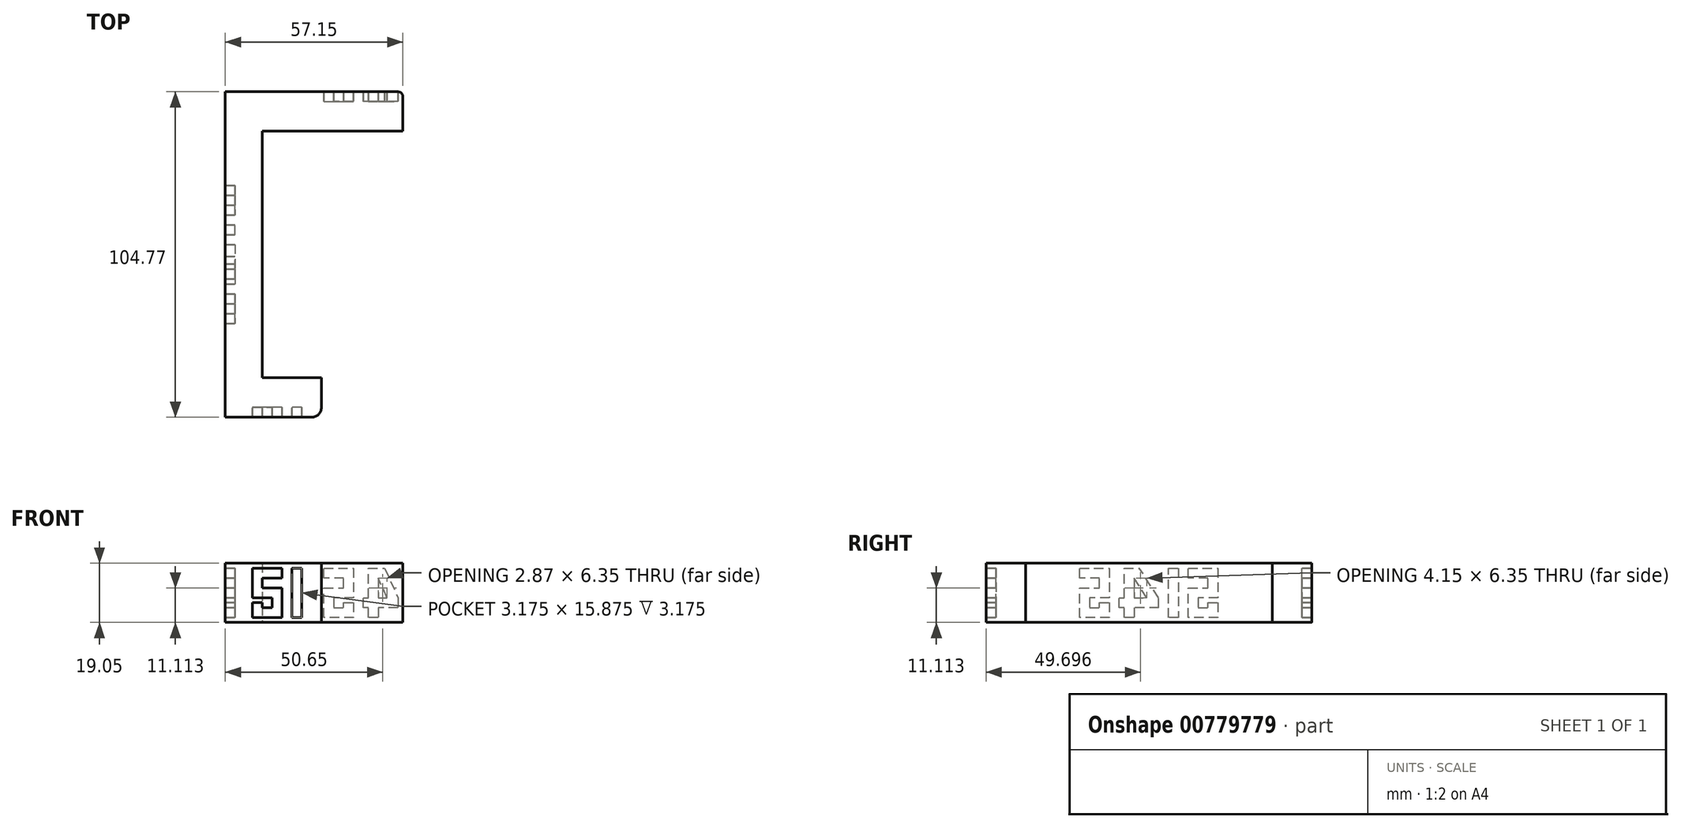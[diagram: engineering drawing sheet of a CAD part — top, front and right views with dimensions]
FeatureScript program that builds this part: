
annotation { "Feature Type Name" : "Feature", "Feature Type Description" : "" }
export const myFeature = defineFeature(function(context is Context, id is Id, definition is map)
    precondition{}
    {
        {
            var Q0;
            Q0=qCreatedBy(makeId("Top.planeOp"),FACE);
            var sketch = newSketch(context, id + "F0", { "sketchPlane" : qUnion([Q0])});
            skLineSegment(sketch, "E0", {"start": v(-101.57, -24.67) * mm, "end": v(-101.57, -129.44) * mm});
            skLineSegment(sketch, "E1", {"start": v(-101.57, -129.44) * mm, "end": v(-69.82, -129.44) * mm});
            skLineSegment(sketch, "E2", {"start": v(-69.82, -129.44) * mm, "end": v(-69.82, -116.74) * mm});
            skLineSegment(sketch, "E3", {"start": v(-69.82, -116.74) * mm, "end": v(-88.87, -116.74) * mm});
            skLineSegment(sketch, "E4", {"start": v(-88.87, -116.74) * mm, "end": v(-88.87, -37.37) * mm});
            skLineSegment(sketch, "E5", {"start": v(-88.87, -37.37) * mm, "end": v(-44.42, -37.37) * mm});
            skLineSegment(sketch, "E6", {"start": v(-44.42, -37.37) * mm, "end": v(-44.42, -24.67) * mm});
            skLineSegment(sketch, "E7", {"start": v(-44.42, -24.67) * mm, "end": v(-101.57, -24.67) * mm});
            skSolve(sketch);
        }
        {
            var Q0;
            Q0=makeQuery(id+"F0.imprint","IMPRINT",FACE,{"disambiguationData":[TD([[makeQuery(id+"F0.imprint","IMPRINT",EDGE,{"derivedFrom":sQuery(id+"F0.wireOp",EDGE,"E0")}),1.0]])]});
            extrude(context, id + "F1", {"entities" : qUnion([Q0]), "depth" : 19.05 * mm, "offsetDistance" : 25.4 * mm});
        }
        {
            var Q0;
            Q0=makeQuery(id+"F1.opExtrude","SWEPT_FACE",FACE,{"disambiguationData":[OSD([sQuery(id+"F0.wireOp",EDGE,"E0")])]});
            var sketch = newSketch(context, id + "F2", { "sketchPlane" : qUnion([Q0])});
            skLineSegment(sketch, "E8", {"start": v(64.35, 17.46) * mm, "end": v(54.83, 17.46) * mm});
            skLineSegment(sketch, "E9", {"start": v(54.83, 17.46) * mm, "end": v(54.83, 7.94) * mm});
            skLineSegment(sketch, "E10", {"start": v(54.83, 7.94) * mm, "end": v(61.18, 7.94) * mm});
            skLineSegment(sketch, "E11", {"start": v(61.18, 7.94) * mm, "end": v(61.18, 4.76) * mm});
            skLineSegment(sketch, "E12", {"start": v(61.18, 4.76) * mm, "end": v(58, 4.76) * mm});
            skLineSegment(sketch, "E13", {"start": v(58, 4.76) * mm, "end": v(58, 6.35) * mm});
            skLineSegment(sketch, "E14", {"start": v(58, 6.35) * mm, "end": v(54.83, 6.35) * mm});
            skLineSegment(sketch, "E15", {"start": v(54.83, 6.35) * mm, "end": v(54.83, 1.59) * mm});
            skLineSegment(sketch, "E16", {"start": v(54.83, 1.59) * mm, "end": v(64.35, 1.59) * mm});
            skLineSegment(sketch, "E17", {"start": v(64.35, 1.59) * mm, "end": v(64.35, 11.11) * mm});
            skLineSegment(sketch, "E18", {"start": v(64.35, 11.11) * mm, "end": v(58, 11.11) * mm});
            skLineSegment(sketch, "E19", {"start": v(58, 11.11) * mm, "end": v(58, 14.29) * mm});
            skLineSegment(sketch, "E20", {"start": v(58, 14.29) * mm, "end": v(64.35, 14.29) * mm});
            skLineSegment(sketch, "E21", {"start": v(64.35, 14.29) * mm, "end": v(64.35, 17.46) * mm});
            skLineSegment(sketch, "E22", {"start": v(67.53, 17.46) * mm, "end": v(67.53, 1.59) * mm});
            skLineSegment(sketch, "E23", {"start": v(67.53, 1.59) * mm, "end": v(70.7, 1.59) * mm});
            skLineSegment(sketch, "E24", {"start": v(70.7, 1.59) * mm, "end": v(70.7, 17.46) * mm});
            skLineSegment(sketch, "E25", {"start": v(70.7, 17.46) * mm, "end": v(67.53, 17.46) * mm});
            skLineSegment(sketch, "E26", {"start": v(85, 17.46) * mm, "end": v(80.1, 17.46) * mm});
            skLineSegment(sketch, "E27", {"start": v(73.88, 4.76) * mm, "end": v(73.88, 4.76) * mm});
            skLineSegment(sketch, "E28", {"start": v(73.88, 4.76) * mm, "end": v(81.82, 4.76) * mm});
            skLineSegment(sketch, "E29", {"start": v(81.82, 4.76) * mm, "end": v(81.82, 1.59) * mm});
            skLineSegment(sketch, "E30", {"start": v(81.82, 1.59) * mm, "end": v(85, 1.59) * mm});
            skLineSegment(sketch, "E31", {"start": v(85, 1.59) * mm, "end": v(85, 4.76) * mm});
            skLineSegment(sketch, "E32", {"start": v(85, 4.76) * mm, "end": v(86.58, 4.76) * mm});
            skLineSegment(sketch, "E33", {"start": v(86.58, 4.76) * mm, "end": v(86.58, 7.94) * mm});
            skLineSegment(sketch, "E34", {"start": v(86.58, 7.94) * mm, "end": v(85, 7.94) * mm});
            skLineSegment(sketch, "E35", {"start": v(85, 7.94) * mm, "end": v(85, 17.46) * mm});
            skLineSegment(sketch, "E36", {"start": v(81.82, 7.94) * mm, "end": v(77.67, 7.94) * mm});
            skLineSegment(sketch, "E37", {"start": v(77.67, 7.94) * mm, "end": v(81.82, 14.29) * mm});
            skLineSegment(sketch, "E38", {"start": v(81.82, 14.29) * mm, "end": v(81.82, 7.94) * mm});
            skLineSegment(sketch, "E39", {"start": v(73.88, 4.76) * mm, "end": v(73.88, 7.94) * mm});
            skLineSegment(sketch, "E40", {"start": v(73.88, 7.94) * mm, "end": v(80.1, 17.46) * mm});
            skLineSegment(sketch, "E41", {"start": v(99.28, 17.46) * mm, "end": v(89.75, 17.46) * mm});
            skLineSegment(sketch, "E42", {"start": v(89.75, 17.46) * mm, "end": v(89.75, 7.94) * mm});
            skLineSegment(sketch, "E43", {"start": v(89.75, 7.94) * mm, "end": v(96.1, 7.94) * mm});
            skLineSegment(sketch, "E44", {"start": v(96.1, 7.94) * mm, "end": v(96.1, 4.76) * mm});
            skLineSegment(sketch, "E45", {"start": v(96.1, 4.76) * mm, "end": v(92.93, 4.76) * mm});
            skPoint(sketch, "E45.endSnap0", {"position": v(92.93, 7.94) * mm});
            skLineSegment(sketch, "E46", {"start": v(92.93, 4.76) * mm, "end": v(92.93, 6.35) * mm});
            skLineSegment(sketch, "E47", {"start": v(92.93, 6.35) * mm, "end": v(89.75, 6.35) * mm});
            skLineSegment(sketch, "E48", {"start": v(89.75, 6.35) * mm, "end": v(89.75, 1.59) * mm});
            skLineSegment(sketch, "E49", {"start": v(89.75, 1.59) * mm, "end": v(99.28, 1.59) * mm});
            skLineSegment(sketch, "E50", {"start": v(99.28, 1.59) * mm, "end": v(99.28, 11.11) * mm});
            skLineSegment(sketch, "E51", {"start": v(99.28, 11.11) * mm, "end": v(92.93, 11.11) * mm});
            skLineSegment(sketch, "E52", {"start": v(92.93, 11.11) * mm, "end": v(92.93, 14.29) * mm});
            skLineSegment(sketch, "E53", {"start": v(92.93, 14.29) * mm, "end": v(99.28, 14.29) * mm});
            skLineSegment(sketch, "E54", {"start": v(99.28, 14.29) * mm, "end": v(99.28, 17.46) * mm});
            skLineSegment(sketch, "E55", {"start": v(99.28, 17.46) * mm, "end": v(126.27, 17.46) * mm});
            skLineSegment(sketch, "E56", {"start": v(54.83, 17.46) * mm, "end": v(27.84, 17.46) * mm});
            skSolve(sketch);
        }
        {
            var Q0;
            Q0=makeQuery(id+"F2.imprint","IMPRINT",FACE,{"disambiguationData":[TD([[makeQuery(id+"F2.imprint","IMPRINT",EDGE,{"derivedFrom":sQuery(id+"F2.wireOp",EDGE,"E8")}),1.0]])]});
            var Q1;
            Q1=makeQuery(id+"F2.imprint","IMPRINT",FACE,{"disambiguationData":[TD([[makeQuery(id+"F2.imprint","IMPRINT",EDGE,{"derivedFrom":sQuery(id+"F2.wireOp",EDGE,"E22")}),1.0]])]});
            var Q2;
            Q2=makeQuery(id+"F2.imprint","IMPRINT",FACE,{"disambiguationData":[TD([[makeQuery(id+"F2.imprint","IMPRINT",EDGE,{"derivedFrom":sQuery(id+"F2.wireOp",EDGE,"E26")}),1.0]])]});
            var Q3;
            Q3=makeQuery(id+"F2.imprint","IMPRINT",FACE,{"disambiguationData":[TD([[makeQuery(id+"F2.imprint","IMPRINT",EDGE,{"derivedFrom":sQuery(id+"F2.wireOp",EDGE,"E41")}),1.0]])]});
            extrude(context, id + "F3", {"entities" : qUnion([Q0, Q1, Q2, Q3]), "operationType" : NewBodyOperationType.REMOVE, "oppositeDirection" : true, "depth" : 3.17 * mm, "offsetDistance" : 25.4 * mm});
        }
        {
            var Q0;
            Q0=makeQuery(id+"F1.opExtrude","SWEPT_FACE",FACE,{"disambiguationData":[OSD([sQuery(id+"F0.wireOp",EDGE,"E1")])]});
            var sketch = newSketch(context, id + "F4", { "sketchPlane" : qUnion([Q0])});
            skLineSegment(sketch, "E57", {"start": v(-82.52, 17.46) * mm, "end": v(-92.04, 17.46) * mm});
            skLineSegment(sketch, "E58", {"start": v(-92.04, 17.46) * mm, "end": v(-92.04, 7.94) * mm});
            skLineSegment(sketch, "E59", {"start": v(-92.04, 7.94) * mm, "end": v(-85.7, 7.94) * mm});
            skLineSegment(sketch, "E60", {"start": v(-85.7, 7.94) * mm, "end": v(-85.7, 4.76) * mm});
            skLineSegment(sketch, "E61", {"start": v(-85.7, 4.76) * mm, "end": v(-88.87, 4.76) * mm});
            skPoint(sketch, "E61.endSnap0", {"position": v(-88.87, 7.94) * mm});
            skLineSegment(sketch, "E62", {"start": v(-88.87, 4.76) * mm, "end": v(-88.87, 6.35) * mm});
            skPoint(sketch, "E62.endSnap0", {"position": v(-85.7, 6.35) * mm});
            skLineSegment(sketch, "E63", {"start": v(-88.87, 6.35) * mm, "end": v(-92.04, 6.35) * mm});
            skLineSegment(sketch, "E64", {"start": v(-92.04, 6.35) * mm, "end": v(-92.04, 1.59) * mm});
            skLineSegment(sketch, "E65", {"start": v(-92.04, 1.59) * mm, "end": v(-82.52, 1.59) * mm});
            skLineSegment(sketch, "E66", {"start": v(-82.52, 1.59) * mm, "end": v(-82.52, 11.11) * mm});
            skLineSegment(sketch, "E67", {"start": v(-82.52, 11.11) * mm, "end": v(-88.87, 11.11) * mm});
            skLineSegment(sketch, "E68", {"start": v(-88.87, 11.11) * mm, "end": v(-88.87, 14.29) * mm});
            skLineSegment(sketch, "E69", {"start": v(-88.87, 14.29) * mm, "end": v(-82.52, 14.29) * mm});
            skLineSegment(sketch, "E70", {"start": v(-82.52, 14.29) * mm, "end": v(-82.52, 17.46) * mm});
            skLineSegment(sketch, "E71", {"start": v(-79.34, 17.46) * mm, "end": v(-79.34, 1.59) * mm});
            skLineSegment(sketch, "E72", {"start": v(-79.34, 1.59) * mm, "end": v(-76.17, 1.59) * mm});
            skLineSegment(sketch, "E73", {"start": v(-76.17, 1.59) * mm, "end": v(-76.17, 17.46) * mm});
            skLineSegment(sketch, "E74", {"start": v(-76.17, 17.46) * mm, "end": v(-79.34, 17.46) * mm});
            skSolve(sketch);
        }
        {
            var Q0;
            Q0=makeQuery(id+"F4.imprint","IMPRINT",FACE,{"disambiguationData":[TD([[makeQuery(id+"F4.imprint","IMPRINT",EDGE,{"derivedFrom":sQuery(id+"F4.wireOp",EDGE,"E57")}),1.0]])]});
            var Q1;
            Q1=makeQuery(id+"F4.imprint","IMPRINT",FACE,{"disambiguationData":[TD([[makeQuery(id+"F4.imprint","IMPRINT",EDGE,{"derivedFrom":sQuery(id+"F4.wireOp",EDGE,"E71")}),1.0]])]});
            extrude(context, id + "F5", {"entities" : qUnion([Q0, Q1]), "operationType" : NewBodyOperationType.REMOVE, "oppositeDirection" : true, "depth" : 3.17 * mm, "offsetDistance" : 25.4 * mm});
        }
        {
            var Q0;
            Q0=makeQuery(id+"F1.opExtrude","SWEPT_FACE",FACE,{"disambiguationData":[OSD([sQuery(id+"F0.wireOp",EDGE,"E6")])]});
            var sketch = newSketch(context, id + "F6", { "sketchPlane" : qUnion([Q0])});
            skLineSegment(sketch, "E75.bottom", {"start": v(-24.67, 0) * mm, "end": v(-37.37, 0) * mm});
            skLineSegment(sketch, "E75.top", {"start": v(-24.67, 19.05) * mm, "end": v(-37.37, 19.05) * mm});
            skLineSegment(sketch, "E75.left", {"start": v(-24.67, 0) * mm, "end": v(-24.67, 19.05) * mm});
            skLineSegment(sketch, "E75.right", {"start": v(-37.37, 0) * mm, "end": v(-37.37, 19.05) * mm});
            skSolve(sketch);
        }
        {
            var Q0;
            Q0 = qSketchRegion(id + "F6", true);
            extrude(context, id + "F7", {"entities" : qUnion([Q0]), "operationType" : NewBodyOperationType.ADD, "depth" : 0.8 * mm, "offsetDistance" : 25.4 * mm});
        }
        {
            var Q0;
            {var subQ6=sQuery(id+"F0.wireOp",EDGE,"E1");var subQ7=sQuery(id+"F0.wireOp",EDGE,"E0");Q0=makeQuery(id+"F3.boolean.opBoolean","SPLIT",FACE,{"disambiguationData":[TD([makeQuery(id+"F1.opExtrude","SWEPT_FACE",FACE,{"disambiguationData":[OSD([subQ6])]})])],"derivedFrom":makeQuery(id+"F1.opExtrude","SWEPT_FACE",FACE,{"disambiguationData":[OSD([subQ7])]})});}
            extrude(context, id + "F8", {"entities" : qUnion([Q0]), "operationType" : NewBodyOperationType.REMOVE, "oppositeDirection" : true, "depth" : 0.8 * mm, "offsetDistance" : 25.4 * mm});
        }
        {
            var Q0;
            Q0=makeQuery(id+"F3.boolean.opBoolean","COPY",FACE,{"derivedFrom":makeQuery(id+"F3.opExtrude","CAP_FACE",FACE,{"disambiguationData":[OSD([sQuery(id+"F2.wireOp",EDGE,"E8"),sQuery(id+"F2.wireOp",EDGE,"E9"),sQuery(id+"F2.wireOp",EDGE,"E10"),sQuery(id+"F2.wireOp",EDGE,"E11"),sQuery(id+"F2.wireOp",EDGE,"E12"),sQuery(id+"F2.wireOp",EDGE,"E13"),sQuery(id+"F2.wireOp",EDGE,"E14"),sQuery(id+"F2.wireOp",EDGE,"E15"),sQuery(id+"F2.wireOp",EDGE,"E16"),sQuery(id+"F2.wireOp",EDGE,"E17"),sQuery(id+"F2.wireOp",EDGE,"E18"),sQuery(id+"F2.wireOp",EDGE,"E19"),sQuery(id+"F2.wireOp",EDGE,"E20"),sQuery(id+"F2.wireOp",EDGE,"E21")])],"isStart":false})});
            var Q1;
            Q1=makeQuery(id+"F3.boolean.opBoolean","COPY",FACE,{"derivedFrom":makeQuery(id+"F3.opExtrude","CAP_FACE",FACE,{"disambiguationData":[OSD([sQuery(id+"F2.wireOp",EDGE,"E22"),sQuery(id+"F2.wireOp",EDGE,"E23"),sQuery(id+"F2.wireOp",EDGE,"E24"),sQuery(id+"F2.wireOp",EDGE,"E25")])],"isStart":false})});
            var Q2;
            Q2=makeQuery(id+"F3.boolean.opBoolean","COPY",FACE,{"derivedFrom":makeQuery(id+"F3.opExtrude","CAP_FACE",FACE,{"disambiguationData":[OSD([sQuery(id+"F2.wireOp",EDGE,"E26"),sQuery(id+"F2.wireOp",EDGE,"E28"),sQuery(id+"F2.wireOp",EDGE,"E29"),sQuery(id+"F2.wireOp",EDGE,"E30"),sQuery(id+"F2.wireOp",EDGE,"E31"),sQuery(id+"F2.wireOp",EDGE,"E32"),sQuery(id+"F2.wireOp",EDGE,"E33"),sQuery(id+"F2.wireOp",EDGE,"E34"),sQuery(id+"F2.wireOp",EDGE,"E35"),sQuery(id+"F2.wireOp",EDGE,"E36"),sQuery(id+"F2.wireOp",EDGE,"E37"),sQuery(id+"F2.wireOp",EDGE,"E38"),sQuery(id+"F2.wireOp",EDGE,"E39"),sQuery(id+"F2.wireOp",EDGE,"E40")])],"isStart":false})});
            var Q3;
            Q3=makeQuery(id+"F3.boolean.opBoolean","COPY",FACE,{"derivedFrom":makeQuery(id+"F3.opExtrude","CAP_FACE",FACE,{"disambiguationData":[OSD([sQuery(id+"F2.wireOp",EDGE,"E41"),sQuery(id+"F2.wireOp",EDGE,"E42"),sQuery(id+"F2.wireOp",EDGE,"E43"),sQuery(id+"F2.wireOp",EDGE,"E44"),sQuery(id+"F2.wireOp",EDGE,"E45"),sQuery(id+"F2.wireOp",EDGE,"E46"),sQuery(id+"F2.wireOp",EDGE,"E47"),sQuery(id+"F2.wireOp",EDGE,"E48"),sQuery(id+"F2.wireOp",EDGE,"E49"),sQuery(id+"F2.wireOp",EDGE,"E50"),sQuery(id+"F2.wireOp",EDGE,"E51"),sQuery(id+"F2.wireOp",EDGE,"E52"),sQuery(id+"F2.wireOp",EDGE,"E53"),sQuery(id+"F2.wireOp",EDGE,"E54")])],"isStart":false})});
            extrude(context, id + "F9", {"entities" : qUnion([Q0, Q1, Q2, Q3]), "operationType" : NewBodyOperationType.REMOVE, "oppositeDirection" : true, "depth" : 0.8 * mm, "offsetDistance" : 25.4 * mm});
        }
        {
            var Q0;
            Q0=makeQuery(id+"F3.boolean.opBoolean","SPLIT",FACE,{"disambiguationData":[TD([makeQuery(id+"F3.opExtrude","SWEPT_FACE",FACE,{"disambiguationData":[OSD([sQuery(id+"F2.wireOp",EDGE,"E36")])]})])],"derivedFrom":makeQuery(id+"F1.opExtrude","SWEPT_FACE",FACE,{"disambiguationData":[OSD([sQuery(id+"F0.wireOp",EDGE,"E0")])]})});
            extrude(context, id + "F10", {"entities" : qUnion([Q0]), "operationType" : NewBodyOperationType.REMOVE, "oppositeDirection" : true, "depth" : 0.8 * mm, "offsetDistance" : 25.4 * mm});
        }
        {
            var Q0;
            Q0=makeQuery(id+"F8.boolean.opBoolean","COPY",EDGE,{"derivedFrom":makeQuery(id+"F8.opExtrude","CAP_EDGE",EDGE,{"disambiguationData":[OSD([sQuery(id+"F0.wireOp",EDGE,"E0"),sQuery(id+"F0.wireOp",EDGE,"E7")])],"isStart":false})});
            var Q1;
            Q1=makeQuery(id+"F8.boolean.opBoolean","COPY",EDGE,{"derivedFrom":makeQuery(id+"F8.opExtrude","CAP_EDGE",EDGE,{"disambiguationData":[OSD([sQuery(id+"F0.wireOp",EDGE,"E0"),sQuery(id+"F0.wireOp",EDGE,"E1")])],"isStart":false})});
            var Q2;
            Q2=makeQuery(id+"F1.opExtrude","SWEPT_EDGE",EDGE,{"disambiguationData":[OSD([sQuery(id+"F0.wireOp",EDGE,"E1"),sQuery(id+"F0.wireOp",EDGE,"E2")])]});
            fillet(context, id + "F11", {"entities" : qUnion([Q0, Q1, Q2]), "radius" : 3.17 * mm, "tangentPropagation" : true, "allowEdgeOverflow" : false});
        }
        {
            var Q0;
            Q0=makeQuery(id+"F9.boolean.opBoolean","COPY",FACE,{"derivedFrom":makeQuery(id+"F9.opExtrude","CAP_FACE",FACE,{"disambiguationData":[OSD([sQuery(id+"F2.wireOp",EDGE,"E8"),sQuery(id+"F2.wireOp",EDGE,"E9"),sQuery(id+"F2.wireOp",EDGE,"E10"),sQuery(id+"F2.wireOp",EDGE,"E11"),sQuery(id+"F2.wireOp",EDGE,"E12"),sQuery(id+"F2.wireOp",EDGE,"E13"),sQuery(id+"F2.wireOp",EDGE,"E14"),sQuery(id+"F2.wireOp",EDGE,"E15"),sQuery(id+"F2.wireOp",EDGE,"E16"),sQuery(id+"F2.wireOp",EDGE,"E17"),sQuery(id+"F2.wireOp",EDGE,"E18"),sQuery(id+"F2.wireOp",EDGE,"E19"),sQuery(id+"F2.wireOp",EDGE,"E20"),sQuery(id+"F2.wireOp",EDGE,"E21")])],"isStart":false})});
            var Q1;
            Q1=makeQuery(id+"F9.boolean.opBoolean","COPY",FACE,{"derivedFrom":makeQuery(id+"F9.opExtrude","CAP_FACE",FACE,{"disambiguationData":[OSD([sQuery(id+"F2.wireOp",EDGE,"E22"),sQuery(id+"F2.wireOp",EDGE,"E23"),sQuery(id+"F2.wireOp",EDGE,"E24"),sQuery(id+"F2.wireOp",EDGE,"E25")])],"isStart":false})});
            var Q2;
            Q2=makeQuery(id+"F9.boolean.opBoolean","COPY",FACE,{"derivedFrom":makeQuery(id+"F9.opExtrude","CAP_FACE",FACE,{"disambiguationData":[OSD([sQuery(id+"F2.wireOp",EDGE,"E26"),sQuery(id+"F2.wireOp",EDGE,"E28"),sQuery(id+"F2.wireOp",EDGE,"E29"),sQuery(id+"F2.wireOp",EDGE,"E30"),sQuery(id+"F2.wireOp",EDGE,"E31"),sQuery(id+"F2.wireOp",EDGE,"E32"),sQuery(id+"F2.wireOp",EDGE,"E33"),sQuery(id+"F2.wireOp",EDGE,"E34"),sQuery(id+"F2.wireOp",EDGE,"E35"),sQuery(id+"F2.wireOp",EDGE,"E36"),sQuery(id+"F2.wireOp",EDGE,"E37"),sQuery(id+"F2.wireOp",EDGE,"E38"),sQuery(id+"F2.wireOp",EDGE,"E39"),sQuery(id+"F2.wireOp",EDGE,"E40")])],"isStart":false})});
            var Q3;
            Q3=makeQuery(id+"F9.boolean.opBoolean","COPY",FACE,{"derivedFrom":makeQuery(id+"F9.opExtrude","CAP_FACE",FACE,{"disambiguationData":[OSD([sQuery(id+"F2.wireOp",EDGE,"E41"),sQuery(id+"F2.wireOp",EDGE,"E42"),sQuery(id+"F2.wireOp",EDGE,"E43"),sQuery(id+"F2.wireOp",EDGE,"E44"),sQuery(id+"F2.wireOp",EDGE,"E45"),sQuery(id+"F2.wireOp",EDGE,"E46"),sQuery(id+"F2.wireOp",EDGE,"E47"),sQuery(id+"F2.wireOp",EDGE,"E48"),sQuery(id+"F2.wireOp",EDGE,"E49"),sQuery(id+"F2.wireOp",EDGE,"E50"),sQuery(id+"F2.wireOp",EDGE,"E51"),sQuery(id+"F2.wireOp",EDGE,"E52"),sQuery(id+"F2.wireOp",EDGE,"E53"),sQuery(id+"F2.wireOp",EDGE,"E54")])],"isStart":false})});
            extrude(context, id + "F12", {"entities" : qUnion([Q0, Q1, Q2, Q3]), "depth" : 3.15 * mm, "offsetDistance" : 25.4 * mm});
        }
        {
            var Q0;
            Q0=makeQuery(id+"F5.boolean.opBoolean","COPY",FACE,{"derivedFrom":makeQuery(id+"F5.opExtrude","CAP_FACE",FACE,{"disambiguationData":[OSD([sQuery(id+"F4.wireOp",EDGE,"E57"),sQuery(id+"F4.wireOp",EDGE,"E58"),sQuery(id+"F4.wireOp",EDGE,"E59"),sQuery(id+"F4.wireOp",EDGE,"E60"),sQuery(id+"F4.wireOp",EDGE,"E61"),sQuery(id+"F4.wireOp",EDGE,"E62"),sQuery(id+"F4.wireOp",EDGE,"E63"),sQuery(id+"F4.wireOp",EDGE,"E64"),sQuery(id+"F4.wireOp",EDGE,"E65"),sQuery(id+"F4.wireOp",EDGE,"E66"),sQuery(id+"F4.wireOp",EDGE,"E67"),sQuery(id+"F4.wireOp",EDGE,"E68"),sQuery(id+"F4.wireOp",EDGE,"E69"),sQuery(id+"F4.wireOp",EDGE,"E70")])],"isStart":false})});
            var Q1;
            Q1=makeQuery(id+"F5.boolean.opBoolean","COPY",FACE,{"derivedFrom":makeQuery(id+"F5.opExtrude","CAP_FACE",FACE,{"disambiguationData":[OSD([sQuery(id+"F4.wireOp",EDGE,"E71"),sQuery(id+"F4.wireOp",EDGE,"E72"),sQuery(id+"F4.wireOp",EDGE,"E73"),sQuery(id+"F4.wireOp",EDGE,"E74")])],"isStart":false})});
            extrude(context, id + "F13", {"entities" : qUnion([Q0, Q1]), "depth" : 3.15 * mm, "offsetDistance" : 25.4 * mm});
        }
        {
            var Q0;
            Q0=makeQuery(id+"F7.opExtrude","CAP_EDGE",EDGE,{"disambiguationData":[OSD([sQuery(id+"F6.wireOp",EDGE,"E75.left")])],"isStart":false});
            fillet(context, id + "F14", {"entities" : qUnion([Q0]), "radius" : 1.59 * mm, "tangentPropagation" : true, "allowEdgeOverflow" : false});
        }
        {
            var Q0;
            Q0=makeQuery(id+"F7.boolean.opBoolean","MERGE",FACE,{"derivedFrom":[makeQuery(id+"F1.opExtrude","SWEPT_FACE",FACE,{"disambiguationData":[OSD([sQuery(id+"F0.wireOp",EDGE,"E7")])]}),makeQuery(id+"F7.opExtrude","SWEPT_FACE",FACE,{"disambiguationData":[OSD([sQuery(id+"F6.wireOp",EDGE,"E75.left")])]})]});
            var sketch = newSketch(context, id + "F15", { "sketchPlane" : qUnion([Q0])});
            skLineSegment(sketch, "E76", {"start": v(45.21, 7.94) * mm, "end": v(45.21, 4.76) * mm});
            skLineSegment(sketch, "E77", {"start": v(45.21, 4.76) * mm, "end": v(51.56, 4.76) * mm});
            skLineSegment(sketch, "E78", {"start": v(51.56, 4.76) * mm, "end": v(51.56, 1.59) * mm});
            skLineSegment(sketch, "E79", {"start": v(51.56, 1.59) * mm, "end": v(54.74, 1.59) * mm});
            skLineSegment(sketch, "E80", {"start": v(54.74, 1.59) * mm, "end": v(54.74, 4.76) * mm});
            skLineSegment(sketch, "E81", {"start": v(54.74, 4.76) * mm, "end": v(56.33, 4.76) * mm});
            skLineSegment(sketch, "E82", {"start": v(56.33, 4.76) * mm, "end": v(56.33, 7.94) * mm});
            skLineSegment(sketch, "E83", {"start": v(56.33, 7.94) * mm, "end": v(54.74, 7.94) * mm});
            skLineSegment(sketch, "E84", {"start": v(54.74, 7.94) * mm, "end": v(54.74, 17.46) * mm});
            skLineSegment(sketch, "E85", {"start": v(54.74, 17.46) * mm, "end": v(49.51, 17.46) * mm});
            skLineSegment(sketch, "E86", {"start": v(49.51, 17.46) * mm, "end": v(45.21, 7.94) * mm});
            skLineSegment(sketch, "E87", {"start": v(51.56, 7.94) * mm, "end": v(48.7, 7.94) * mm});
            skLineSegment(sketch, "E88", {"start": v(48.7, 7.94) * mm, "end": v(51.56, 14.29) * mm});
            skLineSegment(sketch, "E89", {"start": v(51.56, 14.29) * mm, "end": v(51.56, 7.94) * mm});
            skLineSegment(sketch, "E90", {"start": v(69.03, 17.46) * mm, "end": v(59.5, 17.46) * mm});
            skLineSegment(sketch, "E91", {"start": v(59.5, 17.46) * mm, "end": v(59.5, 7.94) * mm});
            skLineSegment(sketch, "E92", {"start": v(59.5, 7.94) * mm, "end": v(65.85, 7.94) * mm});
            skLineSegment(sketch, "E93", {"start": v(65.85, 7.94) * mm, "end": v(65.85, 4.76) * mm});
            skLineSegment(sketch, "E94", {"start": v(65.85, 4.76) * mm, "end": v(62.68, 4.76) * mm});
            skLineSegment(sketch, "E95", {"start": v(62.68, 4.76) * mm, "end": v(62.68, 6.35) * mm});
            skLineSegment(sketch, "E96", {"start": v(62.68, 6.35) * mm, "end": v(59.5, 6.35) * mm});
            skLineSegment(sketch, "E97", {"start": v(59.5, 6.35) * mm, "end": v(59.5, 1.59) * mm});
            skLineSegment(sketch, "E98", {"start": v(59.5, 1.59) * mm, "end": v(69.03, 1.59) * mm});
            skLineSegment(sketch, "E99", {"start": v(69.03, 1.59) * mm, "end": v(69.03, 11.11) * mm});
            skLineSegment(sketch, "E100", {"start": v(69.03, 11.11) * mm, "end": v(62.68, 11.11) * mm});
            skLineSegment(sketch, "E101", {"start": v(62.68, 11.11) * mm, "end": v(62.68, 14.29) * mm});
            skLineSegment(sketch, "E102", {"start": v(62.68, 14.29) * mm, "end": v(69.03, 14.29) * mm});
            skLineSegment(sketch, "E103", {"start": v(69.03, 14.29) * mm, "end": v(69.03, 17.46) * mm});
            skSolve(sketch);
        }
        {
            var Q0;
            Q0=makeQuery(id+"F15.imprint","IMPRINT",FACE,{"disambiguationData":[TD([[makeQuery(id+"F15.imprint","IMPRINT",EDGE,{"derivedFrom":sQuery(id+"F15.wireOp",EDGE,"E76")}),1.0]])]});
            var Q1;
            Q1=makeQuery(id+"F15.imprint","IMPRINT",FACE,{"disambiguationData":[TD([[makeQuery(id+"F15.imprint","IMPRINT",EDGE,{"derivedFrom":sQuery(id+"F15.wireOp",EDGE,"E90")}),1.0]])]});
            extrude(context, id + "F16", {"entities" : qUnion([Q0, Q1]), "operationType" : NewBodyOperationType.REMOVE, "oppositeDirection" : true, "depth" : 3.17 * mm, "offsetDistance" : 25.4 * mm});
        }
        {
            var Q0;
            Q0=makeQuery(id+"F16.boolean.opBoolean","COPY",FACE,{"derivedFrom":makeQuery(id+"F16.opExtrude","CAP_FACE",FACE,{"disambiguationData":[OSD([sQuery(id+"F15.wireOp",EDGE,"E76"),sQuery(id+"F15.wireOp",EDGE,"E77"),sQuery(id+"F15.wireOp",EDGE,"E78"),sQuery(id+"F15.wireOp",EDGE,"E79"),sQuery(id+"F15.wireOp",EDGE,"E80"),sQuery(id+"F15.wireOp",EDGE,"E81"),sQuery(id+"F15.wireOp",EDGE,"E82"),sQuery(id+"F15.wireOp",EDGE,"E83"),sQuery(id+"F15.wireOp",EDGE,"E84"),sQuery(id+"F15.wireOp",EDGE,"E85"),sQuery(id+"F15.wireOp",EDGE,"E86"),sQuery(id+"F15.wireOp",EDGE,"E87"),sQuery(id+"F15.wireOp",EDGE,"E88"),sQuery(id+"F15.wireOp",EDGE,"E89")])],"isStart":false})});
            var Q1;
            Q1=makeQuery(id+"F16.boolean.opBoolean","COPY",FACE,{"derivedFrom":makeQuery(id+"F16.opExtrude","CAP_FACE",FACE,{"disambiguationData":[OSD([sQuery(id+"F15.wireOp",EDGE,"E90"),sQuery(id+"F15.wireOp",EDGE,"E91"),sQuery(id+"F15.wireOp",EDGE,"E92"),sQuery(id+"F15.wireOp",EDGE,"E93"),sQuery(id+"F15.wireOp",EDGE,"E94"),sQuery(id+"F15.wireOp",EDGE,"E95"),sQuery(id+"F15.wireOp",EDGE,"E96"),sQuery(id+"F15.wireOp",EDGE,"E97"),sQuery(id+"F15.wireOp",EDGE,"E98"),sQuery(id+"F15.wireOp",EDGE,"E99"),sQuery(id+"F15.wireOp",EDGE,"E100"),sQuery(id+"F15.wireOp",EDGE,"E101"),sQuery(id+"F15.wireOp",EDGE,"E102"),sQuery(id+"F15.wireOp",EDGE,"E103")])],"isStart":false})});
            extrude(context, id + "F17", {"entities" : qUnion([Q0, Q1]), "depth" : 3.15 * mm, "offsetDistance" : 25.4 * mm});
        }
    });
